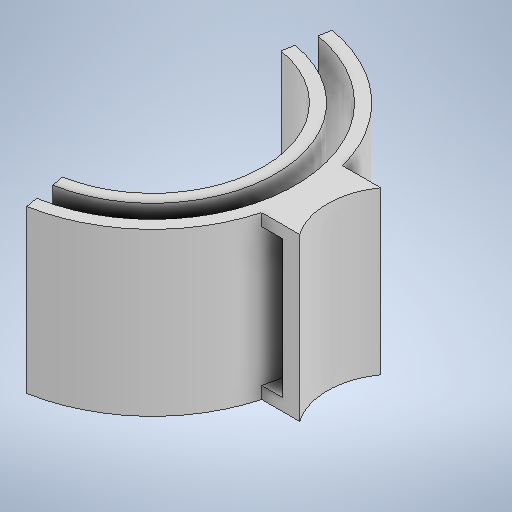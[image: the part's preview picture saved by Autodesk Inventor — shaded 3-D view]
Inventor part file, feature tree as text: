
AUTODESK INVENTOR PART (.ipt)
format: ipt  version: 2025 (Build 290162010, 162A)  size: 286,720 bytes
history: native  units: in
note: dims shown in document units (in); Inventor stores cm internally (conversion verified against a paired STEP export)
features: extrude x5, sketch x5
ambient origin geometry x8: Origin, YZ Plane, XZ Plane, XY Plane, X Axis, Y Axis, Z Axis, Center Point
bodies: Solid1 (feature_tree)
feature tree (10):
  extrude  "Extrusion1"  Depth=3.528in
  extrude  "Extrusion2"  Depth=1.0in TaperAngle=0.0deg
  extrude  "Extrusion3"  Depth=0.1in TaperAngle=0.0deg
  sketch  "Sketch4"  dims[d10=1.0in d11=0.0in d12=1.0in d13=0.0in]
  extrude  "Extrusion4"  Depth=1.0in TaperAngle=0.0deg
  extrude  "Extrusion5"  Depth=2.74in
  sketch  "Sketch1"  dims[d0=3.828in d1=3.528in]
  sketch  "Sketch2"  dims[d2=2.0in d3=0.0in d5=1.0in d6=0.0in]
  sketch  "Sketch3"  dims[d7=3.04in d8=0.1in d9=0.0in]
  sketch  "Sketch5"  dims[d14=3.04in d15=2.74in d17=0.6871in d18=0.6871in]
